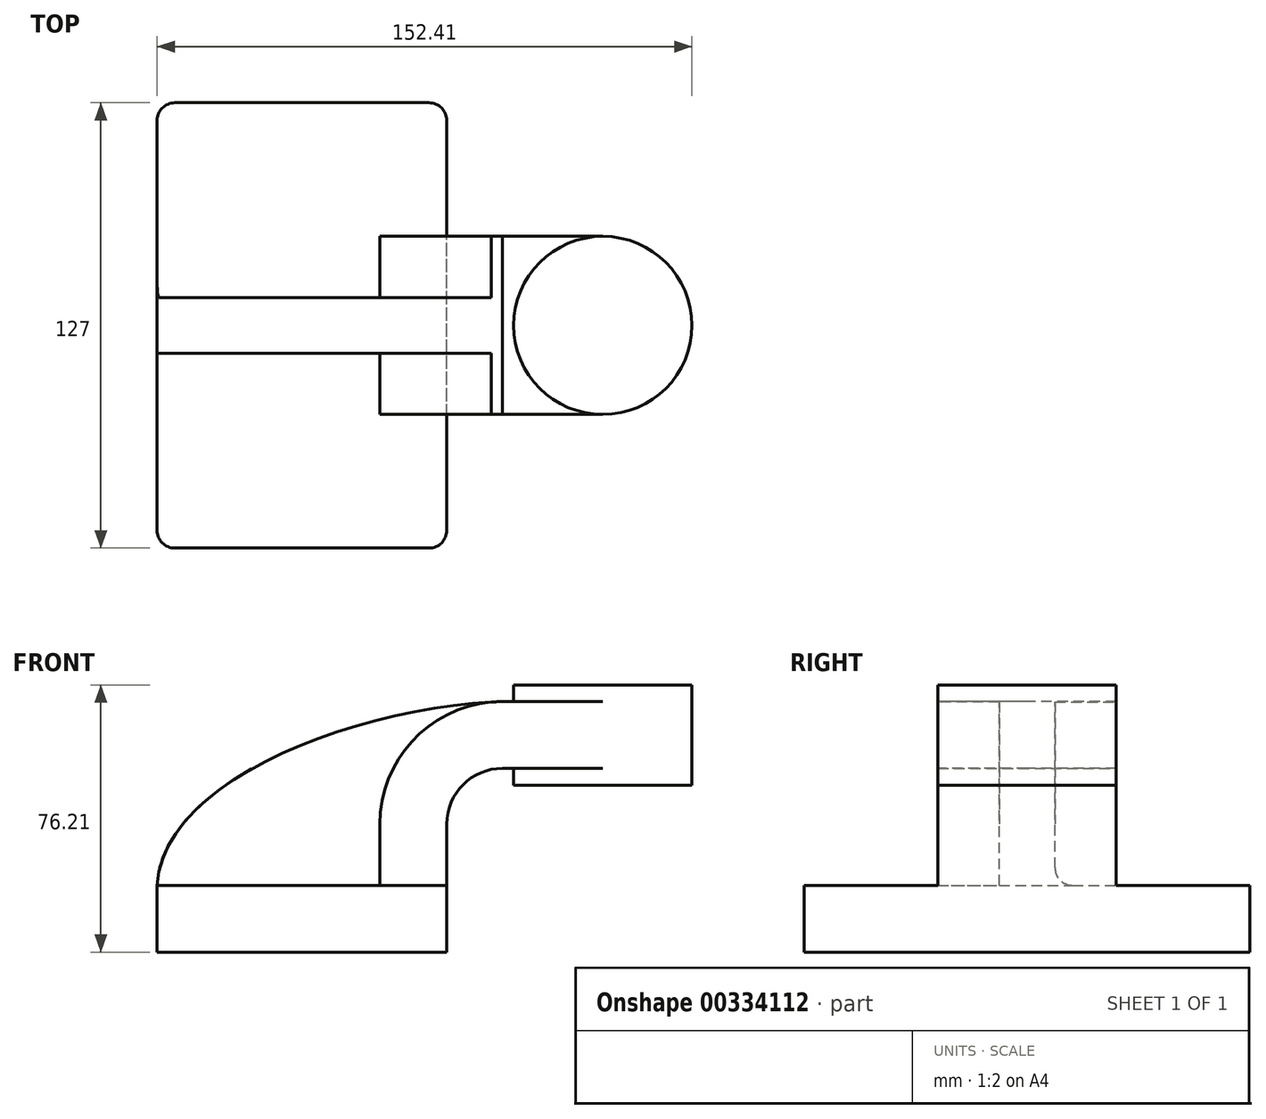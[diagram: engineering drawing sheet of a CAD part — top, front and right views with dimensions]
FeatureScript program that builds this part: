
annotation { "Feature Type Name" : "Feature", "Feature Type Description" : "" }
export const myFeature = defineFeature(function(context is Context, id is Id, definition is map)
    precondition{}
    {
        {
            var Q0;
            Q0=qCreatedBy(makeId("Front.planeOp"),FACE);
            var sketch = newSketch(context, id + "F0", { "sketchPlane" : qUnion([Q0])});
            skLineSegment(sketch, "E0.rect.bottom", {"start": v(-41.28, 9.52) * mm, "end": v(41.28, 9.52) * mm});
            skLineSegment(sketch, "E0.rect.top", {"start": v(-41.28, -9.52) * mm, "end": v(41.28, -9.52) * mm});
            skLineSegment(sketch, "E0.rect.left", {"start": v(-41.28, 9.52) * mm, "end": v(-41.28, -9.52) * mm});
            skLineSegment(sketch, "E0.rect.right", {"start": v(41.28, 9.52) * mm, "end": v(41.28, -9.52) * mm});
            skPoint(sketch, "E0.rect.middle", {"position": v(0, 0) * mm});
            skLineSegment(sketch, "E1", {"start": v(41.28, 9.52) * mm, "end": v(41.28, 27) * mm});
            skArc(sketch, "E2", {"start": v(41.28, 27) * mm, "mid": v(45.92, 38.23) * mm, "end": v(57.15, 42.88) * mm});
            skLineSegment(sketch, "E3", {"start": v(57.15, 42.88) * mm, "end": v(85.72, 42.88) * mm});
            skLineSegment(sketch, "E4.rect.bottom", {"start": v(60.32, 38.1) * mm, "end": v(111.12, 38.1) * mm});
            skLineSegment(sketch, "E4.rect.top", {"start": v(60.32, 66.68) * mm, "end": v(111.12, 66.68) * mm});
            skLineSegment(sketch, "E4.rect.left", {"start": v(60.32, 38.1) * mm, "end": v(60.32, 66.68) * mm});
            skLineSegment(sketch, "E4.rect.right", {"start": v(111.13, 38.1) * mm, "end": v(111.12, 66.68) * mm});
            skPoint(sketch, "E4.rect.middle", {"position": v(85.72, 52.39) * mm});
            skLineSegment(sketch, "E5.0", {"start": v(57.15, 61.93) * mm, "end": v(85.72, 61.93) * mm});
            skArc(sketch, "E5.1", {"start": v(22.23, 27) * mm, "mid": v(32.45, 51.7) * mm, "end": v(57.15, 61.93) * mm});
            skLineSegment(sketch, "E5.2", {"start": v(22.23, 9.52) * mm, "end": v(22.23, 27) * mm});
            skLineSegment(sketch, "E6", {"start": v(85.72, 38.1) * mm, "end": v(85.72, 66.68) * mm});
            skFitSpline(sketch, "E7", {"points": [v(-41.28, 9.53) * mm, v(57.15, 61.93) * mm], "startDerivative": vector(5.2, 92.34) * mm, "endDerivative": vector(120.92, 4.22) * mm});
            skSolve(sketch);
        }
        {
            var Q0;
            Q0=makeQuery(id+"F0.imprint","IMPRINT",FACE,{"disambiguationData":[TD([[makeQuery(id+"F0.imprint","IMPRINT",EDGE,{"derivedFrom":sQuery(id+"F0.wireOp",EDGE,"E0.rect.top")}),1.0]])]});
            extrude(context, id + "F1", {"entities" : qUnion([Q0]), "endBound" : BoundingType.SYMMETRIC, "depth" : 127 * mm});
        }
        {
            var Q0;
            {var subQ9=sQuery(id+"F0.wireOp",EDGE,"E1");Q0=makeQuery(id+"F0.imprint","IMPRINT",FACE,{"disambiguationData":[TD([[makeQuery(id+"F0.imprint","IMPRINT",EDGE,{"derivedFrom":subQ9}),1.0]])]});}
            var Q1;
            {var subQ0=sQuery(id+"F0.wireOp",EDGE,"E6");var subQ1=sQuery(id+"F0.wireOp",EDGE,"E3");var subQ2=makeQuery(id+"F0.imprint","INTERSECT",VERTEX,{"derivedFrom":[subQ1,subQ0]});Q1=makeQuery(id+"F0.imprint","IMPRINT",FACE,{"disambiguationData":[TD([[makeQuery(id+"F0.imprint","IMPRINT",EDGE,{"disambiguationData":[TD([[subQ2,1.0]])],"derivedFrom":subQ1}),1.0]])]});}
            extrude(context, id + "F2", {"entities" : qUnion([Q0, Q1]), "operationType" : NewBodyOperationType.ADD, "endBound" : BoundingType.SYMMETRIC, "depth" : 50.8 * mm});
        }
        {
            var Q0;
            {var subQ3=sQuery(id+"F0.wireOp",EDGE,"E5.2");Q0=makeQuery(id+"F0.imprint","IMPRINT",FACE,{"disambiguationData":[TD([[makeQuery(id+"F0.imprint","IMPRINT",EDGE,{"derivedFrom":subQ3}),1.0]])]});}
            extrude(context, id + "F3", {"entities" : qUnion([Q0]), "operationType" : NewBodyOperationType.ADD, "endBound" : BoundingType.SYMMETRIC, "depth" : 15.88 * mm});
        }
        {
            var Q0;
            {var subQ5=sQuery(id+"F0.wireOp",EDGE,"E4.rect.right");Q0=makeQuery(id+"F0.imprint","IMPRINT",FACE,{"disambiguationData":[TD([[makeQuery(id+"F0.imprint","IMPRINT",EDGE,{"derivedFrom":subQ5}),1.0]])]});}
            var Q1;
            Q1=sQuery(id+"F0.wireOp",EDGE,"E6");
            revolve(context, id + "F4", {"operationType" : NewBodyOperationType.ADD, "entities" : qUnion([Q0]), "axis" : qUnion([Q1]), "revolveType" : RevolveType.FULL});
        }
        {
            var Q0;
            Q0=makeQuery(id+"F1.opExtrude","CAP_EDGE",EDGE,{"disambiguationData":[OSD([sQuery(id+"F0.wireOp",EDGE,"E0.rect.right")])],"isStart":false});
            var Q1;
            Q1=makeQuery(id+"F1.opExtrude","CAP_EDGE",EDGE,{"disambiguationData":[OSD([sQuery(id+"F0.wireOp",EDGE,"E0.rect.left")])],"isStart":false});
            var Q2;
            Q2=makeQuery(id+"F1.opExtrude","CAP_EDGE",EDGE,{"disambiguationData":[OSD([sQuery(id+"F0.wireOp",EDGE,"E0.rect.right")])],"isStart":true});
            var Q3;
            Q3=makeQuery(id+"F1.opExtrude","CAP_EDGE",EDGE,{"disambiguationData":[OSD([sQuery(id+"F0.wireOp",EDGE,"E0.rect.left")])],"isStart":true});
            fillet(context, id + "F5", {"entities" : qUnion([Q0, Q1, Q2, Q3]), "radius" : 5.08 * mm, "tangentPropagation" : true, "allowEdgeOverflow" : false});
        }
        {
            var Q0;
            Q0=makeQuery(id+"F3.opExtrude","CAP_EDGE",EDGE,{"disambiguationData":[OSD([sQuery(id+"F0.wireOp",EDGE,"E0.rect.bottom")])],"isStart":true});
            fillet(context, id + "F6", {"entities" : qUnion([Q0]), "radius" : 5 * mm, "tangentPropagation" : true, "allowEdgeOverflow" : false});
        }
    });
